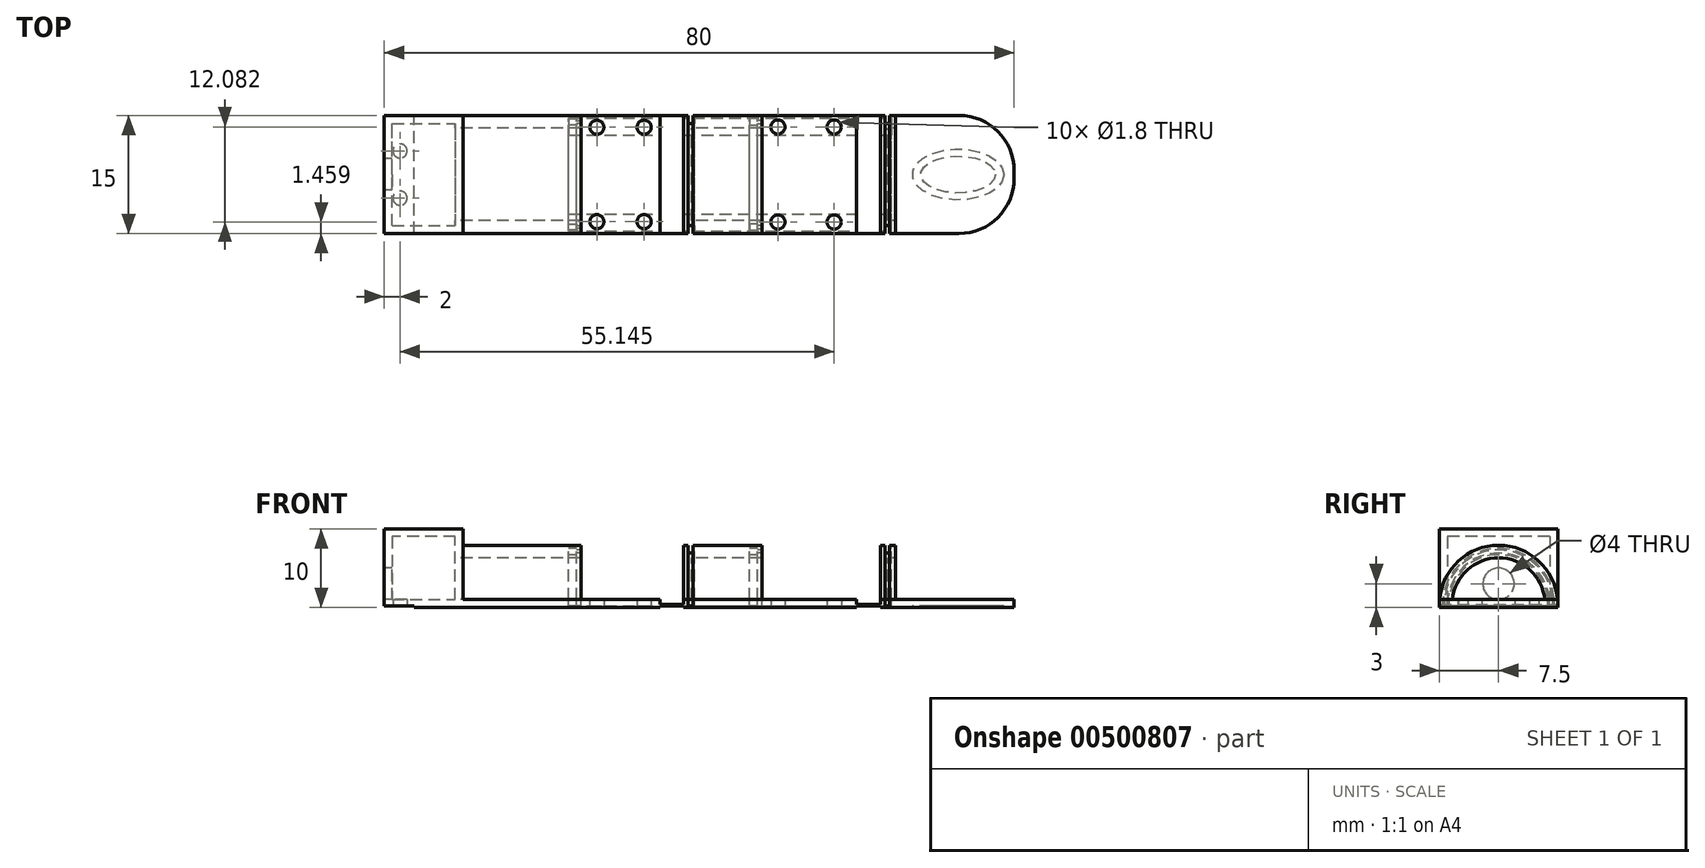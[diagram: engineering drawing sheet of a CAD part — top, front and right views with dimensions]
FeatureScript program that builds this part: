
annotation { "Feature Type Name" : "Feature", "Feature Type Description" : "" }
export const myFeature = defineFeature(function(context is Context, id is Id, definition is map)
    precondition{}
    {
        {
            var Q0;
            Q0=qCreatedBy(makeId("Front.planeOp"),FACE);
            var sketch = newSketch(context, id + "F0", { "sketchPlane" : qUnion([Q0])});
            skLineSegment(sketch, "E0", {"start": v(-10, 0) * mm, "end": v(70, 0) * mm});
            skLineSegment(sketch, "E1", {"start": v(-10, 0) * mm, "end": v(-10, 10) * mm});
            skLineSegment(sketch, "E2", {"start": v(-10, 10) * mm, "end": v(0, 10) * mm});
            skLineSegment(sketch, "E3", {"start": v(0, 10) * mm, "end": v(0, 9) * mm});
            skLineSegment(sketch, "E4", {"start": v(0, 9) * mm, "end": v(-9, 9) * mm});
            skLineSegment(sketch, "E5", {"start": v(-9, 9) * mm, "end": v(-9, 1) * mm});
            skLineSegment(sketch, "E6", {"start": v(-9, 1) * mm, "end": v(25, 1) * mm});
            skLineSegment(sketch, "E7", {"start": v(70, 0) * mm, "end": v(70, 1) * mm});
            skPoint(sketch, "E8.orphan", {"position": v(7.94, 1) * mm});
            skLineSegment(sketch, "E9", {"start": v(25, 1) * mm, "end": v(25, 0.4) * mm});
            skLineSegment(sketch, "E10", {"start": v(25, 0.4) * mm, "end": v(28, 0.4) * mm});
            skLineSegment(sketch, "E11", {"start": v(28, 0.4) * mm, "end": v(28, 1) * mm});
            skLineSegment(sketch, "E12.trimOffspring", {"start": v(28, 1) * mm, "end": v(50, 1) * mm});
            skLineSegment(sketch, "E13", {"start": v(50, 1) * mm, "end": v(50, 0.4) * mm});
            skLineSegment(sketch, "E14", {"start": v(50, 0.4) * mm, "end": v(53, 0.4) * mm});
            skLineSegment(sketch, "E15", {"start": v(53, 0.4) * mm, "end": v(53, 1) * mm});
            skLineSegment(sketch, "E16.trimOffspring", {"start": v(53, 1) * mm, "end": v(70, 1) * mm});
            skSolve(sketch);
        }
        {
            var Q0;
            Q0 = qSketchRegion(id + "F0", true);
            extrude(context, id + "F1", {"entities" : qUnion([Q0]), "endBound" : BoundingType.SYMMETRIC, "depth" : 15 * mm});
        }
        {
            var Q0;
            Q0=qCreatedBy(makeId("Right.planeOp"),FACE);
            var sketch = newSketch(context, id + "F2", { "sketchPlane" : qUnion([Q0])});
            skArc(sketch, "E17", {"start": v(6.5, 0.4) * mm, "mid": v(0, 6.9) * mm, "end": v(-6.5, 0.4) * mm});
            skSolve(sketch);
        }
        {
            var Q0;
            Q0=makeQuery(id+"F1.opExtrude","SWEPT_FACE",FACE,{"disambiguationData":[OSD([sQuery(id+"F0.wireOp",EDGE,"E10")])]});
            var sketch = newSketch(context, id + "F3", { "sketchPlane" : qUnion([Q0])});
            skLineSegment(sketch, "E18.0", {"start": v(0, 7.5) * mm, "end": v(15, 7.5) * mm});
            skLineSegment(sketch, "E19.0", {"start": v(0, 5.9) * mm, "end": v(0, 7.5) * mm});
            skLineSegment(sketch, "E20.0", {"start": v(0, 5.9) * mm, "end": v(15, 5.9) * mm});
            skPoint(sketch, "E21.orphan", {"position": v(-9, 7.5) * mm});
            skPoint(sketch, "E22.orphan", {"position": v(0, -7.5) * mm});
            skLineSegment(sketch, "E23", {"start": v(15, 6.5) * mm, "end": v(15, 5.9) * mm});
            skLineSegment(sketch, "E24", {"start": v(15, 6.5) * mm, "end": v(14.4, 6.5) * mm});
            skLineSegment(sketch, "E25", {"start": v(14.4, 6.5) * mm, "end": v(14.4, 6.3) * mm});
            skLineSegment(sketch, "E26", {"start": v(14.4, 6.3) * mm, "end": v(13.4, 6.3) * mm});
            skLineSegment(sketch, "E27", {"start": v(13.4, 6.3) * mm, "end": v(13.4, 7.1) * mm});
            skLineSegment(sketch, "E28", {"start": v(13.4, 7.1) * mm, "end": v(14.4, 7.1) * mm});
            skLineSegment(sketch, "E29", {"start": v(14.4, 7.1) * mm, "end": v(14.4, 6.9) * mm});
            skLineSegment(sketch, "E30", {"start": v(14.4, 6.9) * mm, "end": v(15, 6.9) * mm});
            skLineSegment(sketch, "E31", {"start": v(15, 6.9) * mm, "end": v(15, 7.5) * mm});
            skPoint(sketch, "E32.orphan", {"position": v(25, 7.5) * mm});
            skLineSegment(sketch, "E33", {"start": v(28, 0) * mm, "end": v(28, 7.5) * mm});
            skLineSegment(sketch, "E34", {"start": v(28, 7.5) * mm, "end": v(28.6, 7.5) * mm});
            skLineSegment(sketch, "E35", {"start": v(38, 7.5) * mm, "end": v(38, 6.9) * mm});
            skLineSegment(sketch, "E36", {"start": v(38, 6.9) * mm, "end": v(37.4, 6.9) * mm});
            skLineSegment(sketch, "E37", {"start": v(37.4, 6.9) * mm, "end": v(37.4, 7.1) * mm});
            skLineSegment(sketch, "E38", {"start": v(37.4, 7.1) * mm, "end": v(36.4, 7.1) * mm});
            skLineSegment(sketch, "E39", {"start": v(36.4, 7.1) * mm, "end": v(36.4, 6.3) * mm});
            skLineSegment(sketch, "E40", {"start": v(36.4, 6.3) * mm, "end": v(37.4, 6.3) * mm});
            skLineSegment(sketch, "E41", {"start": v(37.4, 6.3) * mm, "end": v(37.4, 6.5) * mm});
            skLineSegment(sketch, "E42", {"start": v(37.4, 6.5) * mm, "end": v(38, 6.5) * mm});
            skLineSegment(sketch, "E43", {"start": v(38, 6.5) * mm, "end": v(38, 5.9) * mm});
            skLineSegment(sketch, "E44", {"start": v(38, 5.9) * mm, "end": v(29, 5.9) * mm});
            skLineSegment(sketch, "E45", {"start": v(29, 5.9) * mm, "end": v(29, 0) * mm});
            skLineSegment(sketch, "E46", {"start": v(29, 0) * mm, "end": v(28, 0) * mm});
            skLineSegment(sketch, "E47", {"start": v(29.2, 7.5) * mm, "end": v(29.2, 7.1) * mm});
            skLineSegment(sketch, "E48", {"start": v(29.2, 7.1) * mm, "end": v(29.4, 7.1) * mm});
            skLineSegment(sketch, "E49", {"start": v(29.4, 7.1) * mm, "end": v(29.4, 6.5) * mm});
            skLineSegment(sketch, "E50", {"start": v(29.4, 6.5) * mm, "end": v(28.6, 6.5) * mm});
            skLineSegment(sketch, "E51", {"start": v(28.6, 6.5) * mm, "end": v(28.6, 7.5) * mm});
            skLineSegment(sketch, "E52.trimOffspring", {"start": v(29.2, 7.5) * mm, "end": v(38, 7.5) * mm});
            skLineSegment(sketch, "E53.1.0.0", {"start": v(54, 0) * mm, "end": v(53, 0) * mm});
            skLineSegment(sketch, "E53.1.0.1", {"start": v(53, 0) * mm, "end": v(53, 7.5) * mm});
            skLineSegment(sketch, "E53.1.0.3", {"start": v(54.2, 7.5) * mm, "end": v(54.2, 7.1) * mm});
            skLineSegment(sketch, "E53.1.0.5", {"start": v(54, 5.9) * mm, "end": v(54, 0) * mm});
            skLineSegment(sketch, "E53.1.0.6", {"start": v(53, 7.5) * mm, "end": v(53.6, 7.5) * mm});
            skLineSegment(sketch, "E53.direction1", {"start": v(28, 7.5) * mm, "end": v(53, 7.5) * mm, "construction": true});
            skLineSegment(sketch, "E54.1.0.0", {"start": v(54.2, 7.1) * mm, "end": v(54.4, 7.1) * mm});
            skLineSegment(sketch, "E54.1.0.1", {"start": v(54.4, 6.5) * mm, "end": v(53.6, 6.5) * mm});
            skLineSegment(sketch, "E54.1.0.2", {"start": v(53.6, 6.5) * mm, "end": v(53.6, 7.5) * mm});
            skLineSegment(sketch, "E54.1.0.3", {"start": v(54.4, 7.1) * mm, "end": v(54.4, 6.5) * mm});
            skLineSegment(sketch, "E54.direction1", {"start": v(29.2, 7.1) * mm, "end": v(54.2, 7.1) * mm, "construction": true});
            skLineSegment(sketch, "E55", {"start": v(54, 5.9) * mm, "end": v(54.93, 5.9) * mm});
            skLineSegment(sketch, "E56", {"start": v(54.93, 5.9) * mm, "end": v(54.93, 7.5) * mm});
            skLineSegment(sketch, "E57", {"start": v(54.93, 7.5) * mm, "end": v(54.2, 7.5) * mm});
            skSolve(sketch);
        }
        {
            var Q0;
            Q0 = qSketchRegion(id + "F3", true);
            var Q1;
            Q1=sQuery(id+"F2.wireOp",EDGE,"E17");
            revolve(context, id + "F4", {"operationType" : NewBodyOperationType.ADD, "entities" : qUnion([Q0]), "axis" : qUnion([Q1]), "revolveType" : RevolveType.ONE_DIRECTION, "angle" : 180 * degree});
        }
        {
            var Q0;
            Q0=makeQuery(id+"F1.opExtrude","SWEPT_FACE",FACE,{"disambiguationData":[OSD([sQuery(id+"F0.wireOp",EDGE,"E2")])]});
            var sketch = newSketch(context, id + "F5", { "sketchPlane" : qUnion([Q0])});
            skLineSegment(sketch, "E58.0", {"start": v(-10, -7.5) * mm, "end": v(0, -7.5) * mm});
            skLineSegment(sketch, "E59.0", {"start": v(0, -7.5) * mm, "end": v(0, 7.5) * mm});
            skLineSegment(sketch, "E60.0", {"start": v(-10, 7.5) * mm, "end": v(0, 7.5) * mm});
            skLineSegment(sketch, "E61.0", {"start": v(-10, 6.5) * mm, "end": v(-1, 6.5) * mm});
            skLineSegment(sketch, "E61.1", {"start": v(-1, -6.5) * mm, "end": v(-1, 6.5) * mm});
            skLineSegment(sketch, "E61.2", {"start": v(-10, -6.5) * mm, "end": v(-1, -6.5) * mm});
            skLineSegment(sketch, "E62", {"start": v(-10, 6.5) * mm, "end": v(-10, 7.5) * mm});
            skLineSegment(sketch, "E63", {"start": v(-10, -6.5) * mm, "end": v(-10, -7.5) * mm});
            skSolve(sketch);
        }
        {
            var Q0;
            Q0 = qSketchRegion(id + "F5", true);
            extrude(context, id + "F6", {"entities" : qUnion([Q0]), "operationType" : NewBodyOperationType.ADD, "oppositeDirection" : true, "depth" : 10 * mm});
        }
        {
            var Q0;
            Q0=makeQuery(id+"F6.boolean.opBoolean","SPLIT",FACE,{"derivedFrom":makeQuery(id+"F6.opExtrude","SWEPT_FACE",FACE,{"disambiguationData":[OSD([sQuery(id+"F5.wireOp",EDGE,"E59.0")])]})});
            extrude(context, id + "F7", {"entities" : qUnion([Q0]), "operationType" : NewBodyOperationType.REMOVE, "oppositeDirection" : true, "depth" : 2 * mm});
        }
        {
            var Q0;
            Q0=makeQuery(id+"F1.opExtrude","SWEPT_FACE",FACE,{"disambiguationData":[OSD([sQuery(id+"F0.wireOp",EDGE,"E12.trimOffspring")])]});
            var sketch = newSketch(context, id + "F8", { "sketchPlane" : qUnion([Q0])});
            skLineSegment(sketch, "E64.0", {"start": v(28.6, 6.47) * mm, "end": v(29.4, 6.47) * mm});
            skLineSegment(sketch, "E65.0", {"start": v(29.4, -7.07) * mm, "end": v(29.4, -6.47) * mm});
            skLineSegment(sketch, "E66.0", {"start": v(29.4, 7.07) * mm, "end": v(29.2, 7.07) * mm});
            skLineSegment(sketch, "E67.0", {"start": v(29.2, -7.5) * mm, "end": v(29.2, -7.07) * mm});
            skLineSegment(sketch, "E68.0", {"start": v(28.6, -7.5) * mm, "end": v(28.6, -6.47) * mm});
            skLineSegment(sketch, "E69.0", {"start": v(28.6, 7.5) * mm, "end": v(29.2, 7.5) * mm});
            skLineSegment(sketch, "E70.0", {"start": v(29.4, -6.47) * mm, "end": v(28.6, -6.47) * mm});
            skLineSegment(sketch, "E71.0", {"start": v(29.2, -7.07) * mm, "end": v(29.4, -7.07) * mm});
            skLineSegment(sketch, "E72.0", {"start": v(28.6, -7.5) * mm, "end": v(29.2, -7.5) * mm});
            skLineSegment(sketch, "E73.0", {"start": v(14.4, 7.07) * mm, "end": v(13.4, 7.07) * mm});
            skLineSegment(sketch, "E74.0", {"start": v(13.4, -7.07) * mm, "end": v(13.4, -6.27) * mm});
            skLineSegment(sketch, "E75.0", {"start": v(13.4, 6.27) * mm, "end": v(14.4, 6.27) * mm});
            skLineSegment(sketch, "E76.0", {"start": v(14.4, -7.07) * mm, "end": v(14.4, -6.87) * mm});
            skLineSegment(sketch, "E77.0", {"start": v(15, 6.87) * mm, "end": v(14.4, 6.87) * mm});
            skLineSegment(sketch, "E78.0", {"start": v(14.4, 6.47) * mm, "end": v(15, 6.47) * mm});
            skLineSegment(sketch, "E79.0", {"start": v(15, -6.87) * mm, "end": v(15, -6.47) * mm});
            skLineSegment(sketch, "E80.0", {"start": v(14.4, -6.27) * mm, "end": v(13.4, -6.27) * mm});
            skLineSegment(sketch, "E81.0", {"start": v(15, -6.47) * mm, "end": v(14.4, -6.47) * mm});
            skLineSegment(sketch, "E82.0", {"start": v(14.4, -6.87) * mm, "end": v(15, -6.87) * mm});
            skLineSegment(sketch, "E83.0", {"start": v(13.4, -7.07) * mm, "end": v(14.4, -7.07) * mm});
            skLineSegment(sketch, "E84.0", {"start": v(36.4, -6.27) * mm, "end": v(37.4, -6.27) * mm});
            skLineSegment(sketch, "E85.0", {"start": v(36.4, -7.07) * mm, "end": v(36.4, -6.27) * mm});
            skLineSegment(sketch, "E86.0", {"start": v(37.4, -7.07) * mm, "end": v(36.4, -7.07) * mm});
            skLineSegment(sketch, "E87.0", {"start": v(37.4, -7.07) * mm, "end": v(37.4, -6.87) * mm});
            skLineSegment(sketch, "E88.0", {"start": v(38, -6.87) * mm, "end": v(37.4, -6.87) * mm});
            skLineSegment(sketch, "E89.0", {"start": v(37.4, -6.47) * mm, "end": v(38, -6.47) * mm});
            skLineSegment(sketch, "E90.0", {"start": v(38, -6.87) * mm, "end": v(38, -6.47) * mm});
            skLineSegment(sketch, "E91.0", {"start": v(36.4, 7.07) * mm, "end": v(37.4, 7.07) * mm});
            skLineSegment(sketch, "E92.0", {"start": v(37.4, 6.87) * mm, "end": v(38, 6.87) * mm});
            skLineSegment(sketch, "E93.0", {"start": v(38, 6.47) * mm, "end": v(37.4, 6.47) * mm});
            skLineSegment(sketch, "E94.0", {"start": v(37.4, 6.27) * mm, "end": v(36.4, 6.27) * mm});
            skLineSegment(sketch, "E95.0", {"start": v(53.6, 7.5) * mm, "end": v(54.2, 7.5) * mm});
            skLineSegment(sketch, "E96.0", {"start": v(53.6, -7.5) * mm, "end": v(53.6, -6.47) * mm});
            skLineSegment(sketch, "E97.0", {"start": v(53.6, 6.47) * mm, "end": v(54.4, 6.47) * mm});
            skLineSegment(sketch, "E98.0", {"start": v(54.2, -7.5) * mm, "end": v(54.2, -7.07) * mm});
            skLineSegment(sketch, "E99.0", {"start": v(54.4, 7.07) * mm, "end": v(54.2, 7.07) * mm});
            skLineSegment(sketch, "E100.0", {"start": v(54.4, -7.07) * mm, "end": v(54.4, -6.47) * mm});
            skLineSegment(sketch, "E101.0", {"start": v(54.4, -6.47) * mm, "end": v(53.6, -6.47) * mm});
            skLineSegment(sketch, "E102.0", {"start": v(54.2, -7.07) * mm, "end": v(54.4, -7.07) * mm});
            skLineSegment(sketch, "E103.0", {"start": v(53.6, -7.5) * mm, "end": v(54.2, -7.5) * mm});
            skLineSegment(sketch, "E104.trimOffspring", {"start": v(53.6, 6.47) * mm, "end": v(53.6, 7.5) * mm});
            skLineSegment(sketch, "E105.trimOffspring", {"start": v(54.2, 7.07) * mm, "end": v(54.2, 7.5) * mm});
            skLineSegment(sketch, "E106.trimOffspring", {"start": v(54.4, 6.47) * mm, "end": v(54.4, 7.07) * mm});
            skPoint(sketch, "E107.orphan", {"position": v(53.6, -7.48) * mm});
            skPoint(sketch, "E108.orphan", {"position": v(54.2, -7.48) * mm});
            skPoint(sketch, "E109.orphan", {"position": v(53, -7.5) * mm});
            skPoint(sketch, "E110.orphan", {"position": v(70, -7.5) * mm});
            skPoint(sketch, "E111.orphan", {"position": v(53.6, 7.48) * mm});
            skPoint(sketch, "E112.orphan", {"position": v(53, 7.5) * mm});
            skPoint(sketch, "E113.orphan", {"position": v(70, 7.5) * mm});
            skPoint(sketch, "E114.orphan", {"position": v(38, 7.48) * mm});
            skLineSegment(sketch, "E115.trimOffspring", {"start": v(38, 6.47) * mm, "end": v(38, 6.87) * mm});
            skLineSegment(sketch, "E116.trimOffspring", {"start": v(37.4, 6.27) * mm, "end": v(37.4, 6.47) * mm});
            skLineSegment(sketch, "E117.trimOffspring", {"start": v(36.4, 6.27) * mm, "end": v(36.4, 7.07) * mm});
            skLineSegment(sketch, "E118.trimOffspring", {"start": v(37.4, 6.87) * mm, "end": v(37.4, 7.07) * mm});
            skPoint(sketch, "E119.orphan", {"position": v(38, -7.48) * mm});
            skLineSegment(sketch, "E120.trimOffspring", {"start": v(37.4, -6.47) * mm, "end": v(37.4, -6.27) * mm});
            skLineSegment(sketch, "E121.trimOffspring", {"start": v(29.4, 6.47) * mm, "end": v(29.4, 7.07) * mm});
            skLineSegment(sketch, "E122.trimOffspring", {"start": v(29.2, 7.07) * mm, "end": v(29.2, 7.5) * mm});
            skLineSegment(sketch, "E123.trimOffspring", {"start": v(28.6, 6.47) * mm, "end": v(28.6, 7.5) * mm});
            skPoint(sketch, "E124.orphan", {"position": v(28.6, -7.48) * mm});
            skPoint(sketch, "E125.orphan", {"position": v(29.2, -7.48) * mm});
            skPoint(sketch, "E126.orphan", {"position": v(28, -7.5) * mm});
            skPoint(sketch, "E127.orphan", {"position": v(50, -7.5) * mm});
            skPoint(sketch, "E128.orphan", {"position": v(28.6, 7.48) * mm});
            skPoint(sketch, "E129.orphan", {"position": v(29.2, 7.48) * mm});
            skPoint(sketch, "E130.orphan", {"position": v(28, 7.5) * mm});
            skPoint(sketch, "E131.orphan", {"position": v(50, 7.5) * mm});
            skPoint(sketch, "E132.orphan", {"position": v(15, 7.48) * mm});
            skLineSegment(sketch, "E133.trimOffspring", {"start": v(15, 6.47) * mm, "end": v(15, 6.87) * mm});
            skLineSegment(sketch, "E134.trimOffspring", {"start": v(14.4, 6.27) * mm, "end": v(14.4, 6.47) * mm});
            skLineSegment(sketch, "E135.trimOffspring", {"start": v(13.4, 6.27) * mm, "end": v(13.4, 7.07) * mm});
            skLineSegment(sketch, "E136.trimOffspring", {"start": v(14.4, 6.87) * mm, "end": v(14.4, 7.07) * mm});
            skPoint(sketch, "E137.orphan", {"position": v(15, -7.48) * mm});
            skLineSegment(sketch, "E138.trimOffspring", {"start": v(14.4, -6.47) * mm, "end": v(14.4, -6.27) * mm});
            skPoint(sketch, "E139.orphan", {"position": v(54.2, 7.48) * mm});
            skSolve(sketch);
        }
        {
            var Q0;
            Q0 = qSketchRegion(id + "F8", true);
            extrude(context, id + "F9", {"entities" : qUnion([Q0]), "operationType" : NewBodyOperationType.REMOVE, "oppositeDirection" : true, "depth" : .6 * mm});
        }
        {
            var Q0;
            Q0=makeQuery(id+"F1.opExtrude","SWEPT_FACE",FACE,{"disambiguationData":[OSD([sQuery(id+"F0.wireOp",EDGE,"E0")])]});
            var sketch = newSketch(context, id + "F10", { "sketchPlane" : qUnion([Q0])});
            skLineSegment(sketch, "E140.0", {"start": v(13.4, 7.2) * mm, "end": v(13.4, 5) * mm});
            skLineSegment(sketch, "E141.0", {"start": v(54.4, 7.2) * mm, "end": v(54.4, 5) * mm});
            skLineSegment(sketch, "E142", {"start": v(13.4, 5) * mm, "end": v(25, 5) * mm});
            skLineSegment(sketch, "E143", {"start": v(13.4, 7.2) * mm, "end": v(25, 7.2) * mm});
            skLineSegment(sketch, "E144.MirrorCS", {"start": v(13.4, -7.2) * mm, "end": v(13.4, -5) * mm});
            skLineSegment(sketch, "E145.MirrorCS", {"start": v(13.4, -7.2) * mm, "end": v(25, -7.2) * mm});
            skLineSegment(sketch, "E146.MirrorCS", {"start": v(13.4, -5) * mm, "end": v(25, -5) * mm});
            skLineSegment(sketch, "E147.MirrorCS", {"start": v(54.4, -7.2) * mm, "end": v(54.4, -5) * mm});
            skLineSegment(sketch, "E148.0", {"start": v(25, 7.5) * mm, "end": v(25, 7.2) * mm});
            skLineSegment(sketch, "E149.0", {"start": v(28, 7.5) * mm, "end": v(28, 7.2) * mm});
            skLineSegment(sketch, "E150.0", {"start": v(50, 7.5) * mm, "end": v(50, 7.2) * mm});
            skLineSegment(sketch, "E151.0", {"start": v(53, 7.5) * mm, "end": v(53, 7.2) * mm});
            skLineSegment(sketch, "E152.0", {"start": v(25, 7.5) * mm, "end": v(28, 7.5) * mm});
            skLineSegment(sketch, "E153.0", {"start": v(25, -7.5) * mm, "end": v(28, -7.5) * mm});
            skPoint(sketch, "E154.orphan", {"position": v(-10, -7.5) * mm});
            skPoint(sketch, "E155.orphan", {"position": v(-10, 7.5) * mm});
            skPoint(sketch, "E156.orphan", {"position": v(70, 7.5) * mm});
            skPoint(sketch, "E157.orphan", {"position": v(70, -7.5) * mm});
            skLineSegment(sketch, "E158.trimOffspring", {"start": v(50, -7.5) * mm, "end": v(53, -7.5) * mm});
            skLineSegment(sketch, "E159.trimOffspring", {"start": v(53, -7.2) * mm, "end": v(54.4, -7.2) * mm});
            skLineSegment(sketch, "E160.trimOffspring", {"start": v(53, -7.2) * mm, "end": v(53, -7.5) * mm});
            skLineSegment(sketch, "E161.trimOffspring", {"start": v(50, -7.2) * mm, "end": v(50, -7.5) * mm});
            skLineSegment(sketch, "E162.trimOffspring", {"start": v(53, -5) * mm, "end": v(54.4, -5) * mm});
            skLineSegment(sketch, "E163.trimOffspring", {"start": v(53, 5) * mm, "end": v(54.4, 5) * mm});
            skLineSegment(sketch, "E164.trimOffspring", {"start": v(53, 7.2) * mm, "end": v(54.4, 7.2) * mm});
            skLineSegment(sketch, "E165.trimOffspring", {"start": v(53, 5) * mm, "end": v(53, -5) * mm});
            skLineSegment(sketch, "E166.trimOffspring", {"start": v(50, 5) * mm, "end": v(50, -5) * mm});
            skLineSegment(sketch, "E167.trimOffspring", {"start": v(50, 7.5) * mm, "end": v(53, 7.5) * mm});
            skLineSegment(sketch, "E168.trimOffspring", {"start": v(28, 5) * mm, "end": v(50, 5) * mm});
            skLineSegment(sketch, "E169.trimOffspring", {"start": v(28, 7.2) * mm, "end": v(50, 7.2) * mm});
            skLineSegment(sketch, "E170.trimOffspring", {"start": v(28, 5) * mm, "end": v(28, -5) * mm});
            skLineSegment(sketch, "E171.trimOffspring", {"start": v(25, 5) * mm, "end": v(25, -5) * mm});
            skLineSegment(sketch, "E172.trimOffspring", {"start": v(28, -5) * mm, "end": v(50, -5) * mm});
            skLineSegment(sketch, "E173.trimOffspring", {"start": v(25, -7.2) * mm, "end": v(25, -7.5) * mm});
            skLineSegment(sketch, "E174.trimOffspring", {"start": v(28, -7.2) * mm, "end": v(28, -7.5) * mm});
            skLineSegment(sketch, "E175.trimOffspring", {"start": v(28, -7.2) * mm, "end": v(50, -7.2) * mm});
            skEllipse(sketch, "E176", {"center": v(62.89, 0) * mm, "majorRadius": 4.74 * mm, "minorRadius": 2.33 * mm, "majorAxis": v(1, 0)});
            skEllipse(sketch, "E177", {"center": v(62.89, 0) * mm, "majorRadius": 5.8 * mm, "minorRadius": 3.24 * mm, "majorAxis": v(1, 0)});
            skLineSegment(sketch, "E178.bottom", {"start": v(-10, 7.5) * mm, "end": v(-6.2, 7.5) * mm});
            skLineSegment(sketch, "E178.top", {"start": v(-10, -7.5) * mm, "end": v(-6.2, -7.5) * mm});
            skLineSegment(sketch, "E178.left", {"start": v(-10, 7.5) * mm, "end": v(-10, -7.5) * mm});
            skLineSegment(sketch, "E178.right", {"start": v(-6.2, 7.5) * mm, "end": v(-6.2, -7.5) * mm});
            skSolve(sketch);
        }
        {
            var Q0;
            Q0 = qSketchRegion(id + "F10", true);
            extrude(context, id + "F11", {"entities" : qUnion([Q0]), "operationType" : NewBodyOperationType.REMOVE, "oppositeDirection" : true, "depth" : .2 * mm});
        }
        {
            var Q0;
            Q0=makeQuery(id+"F11.boolean.opBoolean","COPY",FACE,{"derivedFrom":makeQuery(id+"F11.opExtrude","CAP_FACE",FACE,{"disambiguationData":[OSD([sQuery(id+"F10.wireOp",EDGE,"E140.0"),sQuery(id+"F10.wireOp",EDGE,"E141.0"),sQuery(id+"F10.wireOp",EDGE,"mV5M2w9i-R190-RHtX-cRMj-KFKyZSCLrJQd"),sQuery(id+"F10.wireOp",EDGE,"ou8x8EIK-e10T-fSeT-XhqI-Fwk7xwms1ylR")])],"isStart":false})});
            var sketch = newSketch(context, id + "F12", { "sketchPlane" : qUnion([Q0])});
            skCircle(sketch, "E179", {"center": v(17, 6) * mm, "radius": 0.9 * mm});
            skCircle(sketch, "E180.1.0.0", {"center": v(23, 6) * mm, "radius": 0.9 * mm});
            skLineSegment(sketch, "E180.direction1", {"start": v(17, 6) * mm, "end": v(23, 6) * mm, "construction": true});
            skCircle(sketch, "E181.1.0.0", {"center": v(40, 6.04) * mm, "radius": 0.9 * mm});
            skLineSegment(sketch, "E181.direction1", {"start": v(17, 6) * mm, "end": v(40, 6.04) * mm, "construction": true});
            skCircle(sketch, "E182.1.0.0", {"center": v(47.15, 6.04) * mm, "radius": 0.9 * mm});
            skLineSegment(sketch, "E182.direction1", {"start": v(40, 6.04) * mm, "end": v(47.15, 6.04) * mm, "construction": true});
            skCircle(sketch, "E183.MirrorC", {"center": v(23, -6) * mm, "radius": 0.9 * mm});
            skCircle(sketch, "E184.MirrorC", {"center": v(17, -6) * mm, "radius": 0.9 * mm});
            skCircle(sketch, "E185.MirrorC", {"center": v(40, -6.04) * mm, "radius": 0.9 * mm});
            skCircle(sketch, "E186.MirrorC", {"center": v(47.15, -6.04) * mm, "radius": 0.9 * mm});
            skCircle(sketch, "E187", {"center": v(-8, 3) * mm, "radius": 0.9 * mm});
            skCircle(sketch, "E188.MirrorC", {"center": v(-8, -3) * mm, "radius": 0.9 * mm});
            skSolve(sketch);
        }
        {
            var Q0;
            Q0 = qSketchRegion(id + "F12", true);
            extrude(context, id + "F13", {"entities" : qUnion([Q0]), "operationType" : NewBodyOperationType.REMOVE, "oppositeDirection" : true, "depth" : 3 * mm});
        }
        {
            var Q0;
            Q0=makeQuery(id+"F9.boolean.opBoolean","COPY",FACE,{"derivedFrom":makeQuery(id+"F9.opExtrude","CAP_FACE",FACE,{"disambiguationData":[OSD([sQuery(id+"F8.wireOp",EDGE,"E91.0"),sQuery(id+"F8.wireOp",EDGE,"E92.0"),sQuery(id+"F8.wireOp",EDGE,"E93.0"),sQuery(id+"F8.wireOp",EDGE,"E94.0"),sQuery(id+"F8.wireOp",EDGE,"E115.trimOffspring"),sQuery(id+"F8.wireOp",EDGE,"E116.trimOffspring"),sQuery(id+"F8.wireOp",EDGE,"E117.trimOffspring"),sQuery(id+"F8.wireOp",EDGE,"E118.trimOffspring")])],"isStart":false})});
            var Q1;
            Q1=makeQuery(id+"F9.boolean.opBoolean","COPY",FACE,{"derivedFrom":makeQuery(id+"F9.opExtrude","CAP_FACE",FACE,{"disambiguationData":[OSD([sQuery(id+"F8.wireOp",EDGE,"E84.0"),sQuery(id+"F8.wireOp",EDGE,"E85.0"),sQuery(id+"F8.wireOp",EDGE,"E86.0"),sQuery(id+"F8.wireOp",EDGE,"E87.0"),sQuery(id+"F8.wireOp",EDGE,"E88.0"),sQuery(id+"F8.wireOp",EDGE,"E89.0"),sQuery(id+"F8.wireOp",EDGE,"E90.0"),sQuery(id+"F8.wireOp",EDGE,"E120.trimOffspring")])],"isStart":false})});
            var Q2;
            Q2=makeQuery(id+"F9.boolean.opBoolean","COPY",FACE,{"derivedFrom":makeQuery(id+"F9.opExtrude","CAP_FACE",FACE,{"disambiguationData":[OSD([sQuery(id+"F8.wireOp",EDGE,"E65.0"),sQuery(id+"F8.wireOp",EDGE,"E67.0"),sQuery(id+"F8.wireOp",EDGE,"E68.0"),sQuery(id+"F8.wireOp",EDGE,"E70.0"),sQuery(id+"F8.wireOp",EDGE,"E71.0"),sQuery(id+"F8.wireOp",EDGE,"E72.0")])],"isStart":false})});
            var Q3;
            Q3=makeQuery(id+"F9.boolean.opBoolean","COPY",FACE,{"derivedFrom":makeQuery(id+"F9.opExtrude","CAP_FACE",FACE,{"disambiguationData":[OSD([sQuery(id+"F8.wireOp",EDGE,"E74.0"),sQuery(id+"F8.wireOp",EDGE,"E76.0"),sQuery(id+"F8.wireOp",EDGE,"E79.0"),sQuery(id+"F8.wireOp",EDGE,"E80.0"),sQuery(id+"F8.wireOp",EDGE,"E81.0"),sQuery(id+"F8.wireOp",EDGE,"E82.0"),sQuery(id+"F8.wireOp",EDGE,"E83.0"),sQuery(id+"F8.wireOp",EDGE,"E138.trimOffspring")])],"isStart":false})});
            var Q4;
            Q4=makeQuery(id+"F9.boolean.opBoolean","COPY",FACE,{"derivedFrom":makeQuery(id+"F9.opExtrude","CAP_FACE",FACE,{"disambiguationData":[OSD([sQuery(id+"F8.wireOp",EDGE,"E73.0"),sQuery(id+"F8.wireOp",EDGE,"E75.0"),sQuery(id+"F8.wireOp",EDGE,"E77.0"),sQuery(id+"F8.wireOp",EDGE,"E78.0"),sQuery(id+"F8.wireOp",EDGE,"E133.trimOffspring"),sQuery(id+"F8.wireOp",EDGE,"E134.trimOffspring"),sQuery(id+"F8.wireOp",EDGE,"E135.trimOffspring"),sQuery(id+"F8.wireOp",EDGE,"E136.trimOffspring")])],"isStart":false})});
            var Q5;
            Q5=makeQuery(id+"F9.boolean.opBoolean","COPY",FACE,{"derivedFrom":makeQuery(id+"F9.opExtrude","CAP_FACE",FACE,{"disambiguationData":[OSD([sQuery(id+"F8.wireOp",EDGE,"E64.0"),sQuery(id+"F8.wireOp",EDGE,"E66.0"),sQuery(id+"F8.wireOp",EDGE,"E69.0"),sQuery(id+"F8.wireOp",EDGE,"E121.trimOffspring"),sQuery(id+"F8.wireOp",EDGE,"E122.trimOffspring"),sQuery(id+"F8.wireOp",EDGE,"E123.trimOffspring")])],"isStart":false})});
            var Q6;
            Q6=makeQuery(id+"F9.boolean.opBoolean","COPY",FACE,{"derivedFrom":makeQuery(id+"F9.opExtrude","CAP_FACE",FACE,{"disambiguationData":[OSD([sQuery(id+"F8.wireOp",EDGE,"E95.0"),sQuery(id+"F8.wireOp",EDGE,"E97.0"),sQuery(id+"F8.wireOp",EDGE,"E99.0"),sQuery(id+"F8.wireOp",EDGE,"E104.trimOffspring"),sQuery(id+"F8.wireOp",EDGE,"E105.trimOffspring"),sQuery(id+"F8.wireOp",EDGE,"E106.trimOffspring")])],"isStart":false})});
            var Q7;
            Q7=makeQuery(id+"F9.boolean.opBoolean","COPY",FACE,{"derivedFrom":makeQuery(id+"F9.opExtrude","CAP_FACE",FACE,{"disambiguationData":[OSD([sQuery(id+"F8.wireOp",EDGE,"E96.0"),sQuery(id+"F8.wireOp",EDGE,"E98.0"),sQuery(id+"F8.wireOp",EDGE,"E100.0"),sQuery(id+"F8.wireOp",EDGE,"E101.0"),sQuery(id+"F8.wireOp",EDGE,"E102.0"),sQuery(id+"F8.wireOp",EDGE,"E103.0")])],"isStart":false})});
            extrude(context, id + "F14", {"entities" : qUnion([Q0, Q1, Q2, Q3, Q4, Q5, Q6, Q7]), "operationType" : NewBodyOperationType.REMOVE, "oppositeDirection" : true, "depth" : 25 * mm});
        }
        {
            var Q0;
            Q0=makeQuery(id+"F1.opExtrude","CAP_EDGE",EDGE,{"disambiguationData":[OSD([sQuery(id+"F0.wireOp",EDGE,"E7")])],"isStart":false});
            var Q1;
            Q1=makeQuery(id+"F1.opExtrude","CAP_EDGE",EDGE,{"disambiguationData":[OSD([sQuery(id+"F0.wireOp",EDGE,"E7")])],"isStart":true});
            fillet(context, id + "F15", {"entities" : qUnion([Q0, Q1]), "radius" : 7 * mm, "tangentPropagation" : true, "allowEdgeOverflow" : false});
        }
        {
            var Q0;
            Q0=makeQuery(id+"F1.opExtrude","SWEPT_FACE",FACE,{"disambiguationData":[OSD([sQuery(id+"F0.wireOp",EDGE,"E1")])]});
            var sketch = newSketch(context, id + "F16", { "sketchPlane" : qUnion([Q0])});
            skCircle(sketch, "E189", {"center": v(0, 3) * mm, "radius": 2 * mm});
            skSolve(sketch);
        }
        {
            var Q0;
            Q0 = qSketchRegion(id + "F16", true);
            extrude(context, id + "F17", {"entities" : qUnion([Q0]), "operationType" : NewBodyOperationType.REMOVE, "oppositeDirection" : true, "depth" : 2 * mm});
        }
    });
